# Revit family: Hand_Shower_Extension-Grohe-Retro_Fit-26464_Series
name_source: partatom
category: Specialty Equipment
units: mm (PartAtom-declared; Revit-internal decimal feet)

## family parameters
Always vertical = No
Cut with Voids When Loaded = No
OmniClass Number = 23.45.05.14.17
OmniClass Title = Showers
Part Type = Normal
Room Calculation Point = No
Round Connector Dimension = Use Diameter
Shared = Yes
Work Plane-Based = Yes

## types (2) — shared parameters
ASME A112.18.1/CSA B125.1 = Yes
Assembly Code = D2010710
CEC Compliant = Yes
Default Elevation = 0"
Description = Retro-Fit 6-inch Height Extension
Height = 7 25/32"
Installation Instruction Link = https://americanstandard.box.com
Length = 7/8"
Manufacturer = GROHE
Price = Prices may vary. Please consult Manufacturer Representative for most up-to-date price list.
Product Documentation Link = https://americanstandard.box.com
Product Page URL = https://www.grohe.us
Revised Date = 11/01/2021
URL = https://www.grohe.us
US Federal and State material regulations = Yes
Width = 7/8"

## per-type parameters (varying)
| type | Finish | Material |
| 26464000 | Metal-Grohe-000-StarLight Chrome | Metal-Grohe-000-Chrome |
| 26464EN0 | Metal-Grohe-EN0-Brushed Nickel Infinity Finish | Metal-Grohe-EN0-Brushed Nickel Infinity Finish |

note: column(s) folded — value = type name in every type: Model

## geometry (parser evidence)
native form markers: Sweep x2
no freeform markers — native parametric forms only
